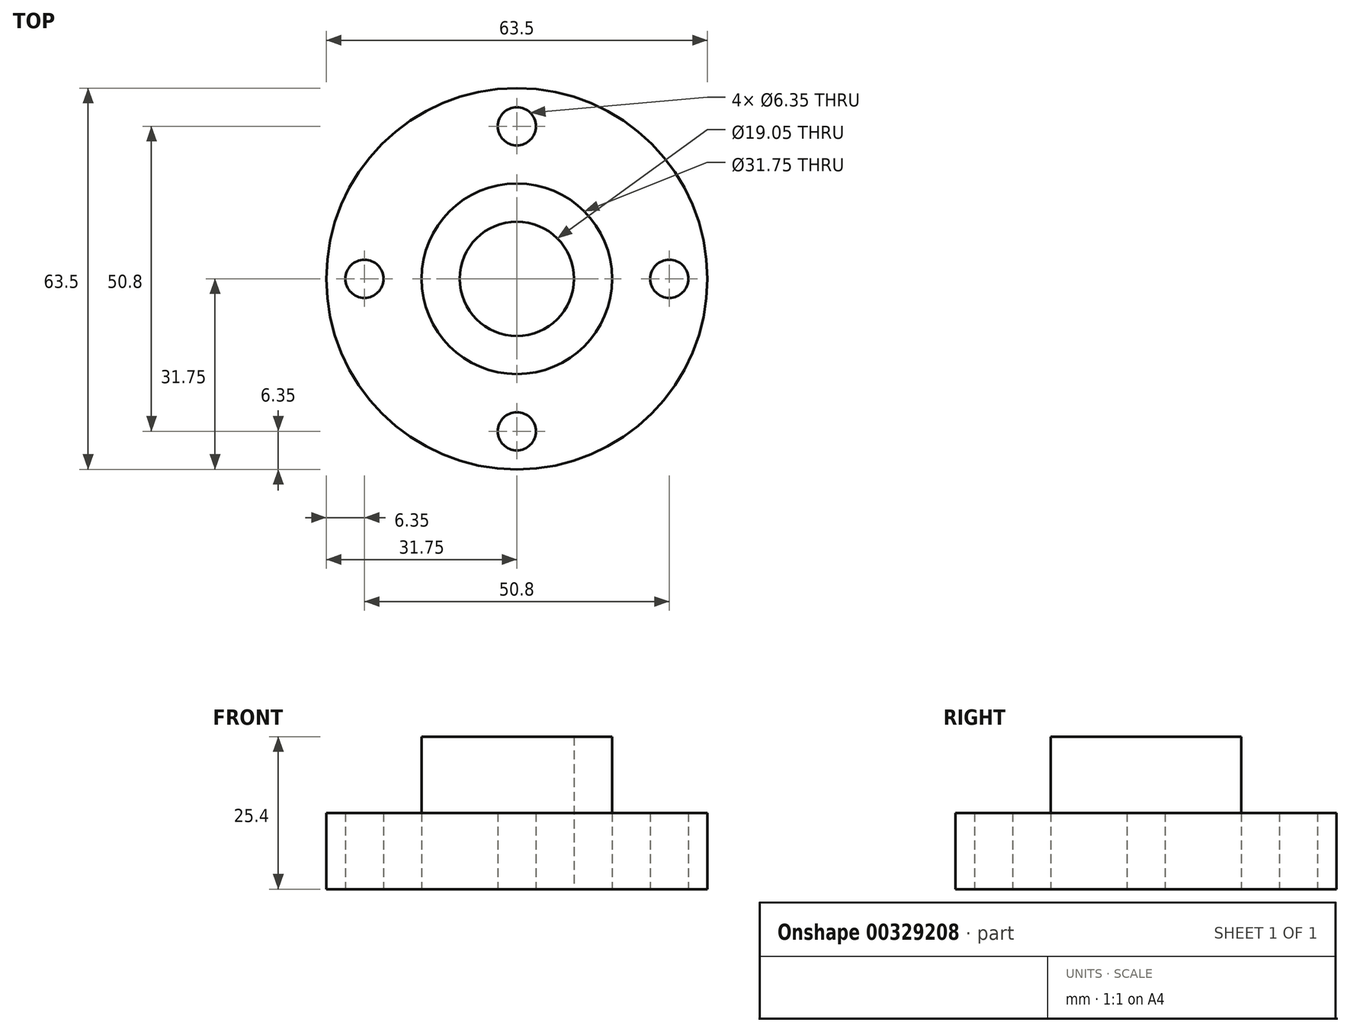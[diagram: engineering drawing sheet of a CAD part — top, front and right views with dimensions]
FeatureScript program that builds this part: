
annotation { "Feature Type Name" : "Feature", "Feature Type Description" : "" }
export const myFeature = defineFeature(function(context is Context, id is Id, definition is map)
    precondition{}
    {
        {
            var Q0;
            Q0=qCreatedBy(makeId("Top.planeOp"),FACE);
            var sketch = newSketch(context, id + "F0", { "sketchPlane" : qUnion([Q0])});
            skCircle(sketch, "E0", {"center": v(0, 0) * mm, "radius": 31.75 * mm});
            skCircle(sketch, "E1", {"center": v(0, 0) * mm, "radius": 15.88 * mm});
            skCircle(sketch, "E2", {"center": v(0, 0) * mm, "radius": 9.53 * mm});
            skCircle(sketch, "E3", {"center": v(0, 25.4) * mm, "radius": 3.18 * mm});
            skCircle(sketch, "E4", {"center": v(25.4, 0) * mm, "radius": 3.18 * mm});
            skCircle(sketch, "E5", {"center": v(-25.4, 0) * mm, "radius": 3.18 * mm});
            skCircle(sketch, "E6", {"center": v(0, -25.4) * mm, "radius": 3.18 * mm});
            skFitSpline(sketch, "E7", {"points": [v(0, 25.4) * mm, v(25.4, 0) * mm, v(0, -25.4) * mm, v(-25.4, 0) * mm, v(0, 25.4) * mm], "construction": true});
            skSolve(sketch);
        }
        {
            var Q0;
            Q0 = qSketchRegion(id + "F0", true);
            extrude(context, id + "F1", {"entities" : qUnion([Q0]), "depth" : 12.7 * mm});
        }
        {
            var Q0;
            Q0=makeQuery(id+"F0.imprint","IMPRINT",FACE,{"disambiguationData":[TD([[makeQuery(id+"F0.imprint","IMPRINT",EDGE,{"derivedFrom":sQuery(id+"F0.wireOp",EDGE,"E1")}),1.0]])]});
            extrude(context, id + "F2", {"entities" : qUnion([Q0]), "depth" : 25.4 * mm});
        }
    });
